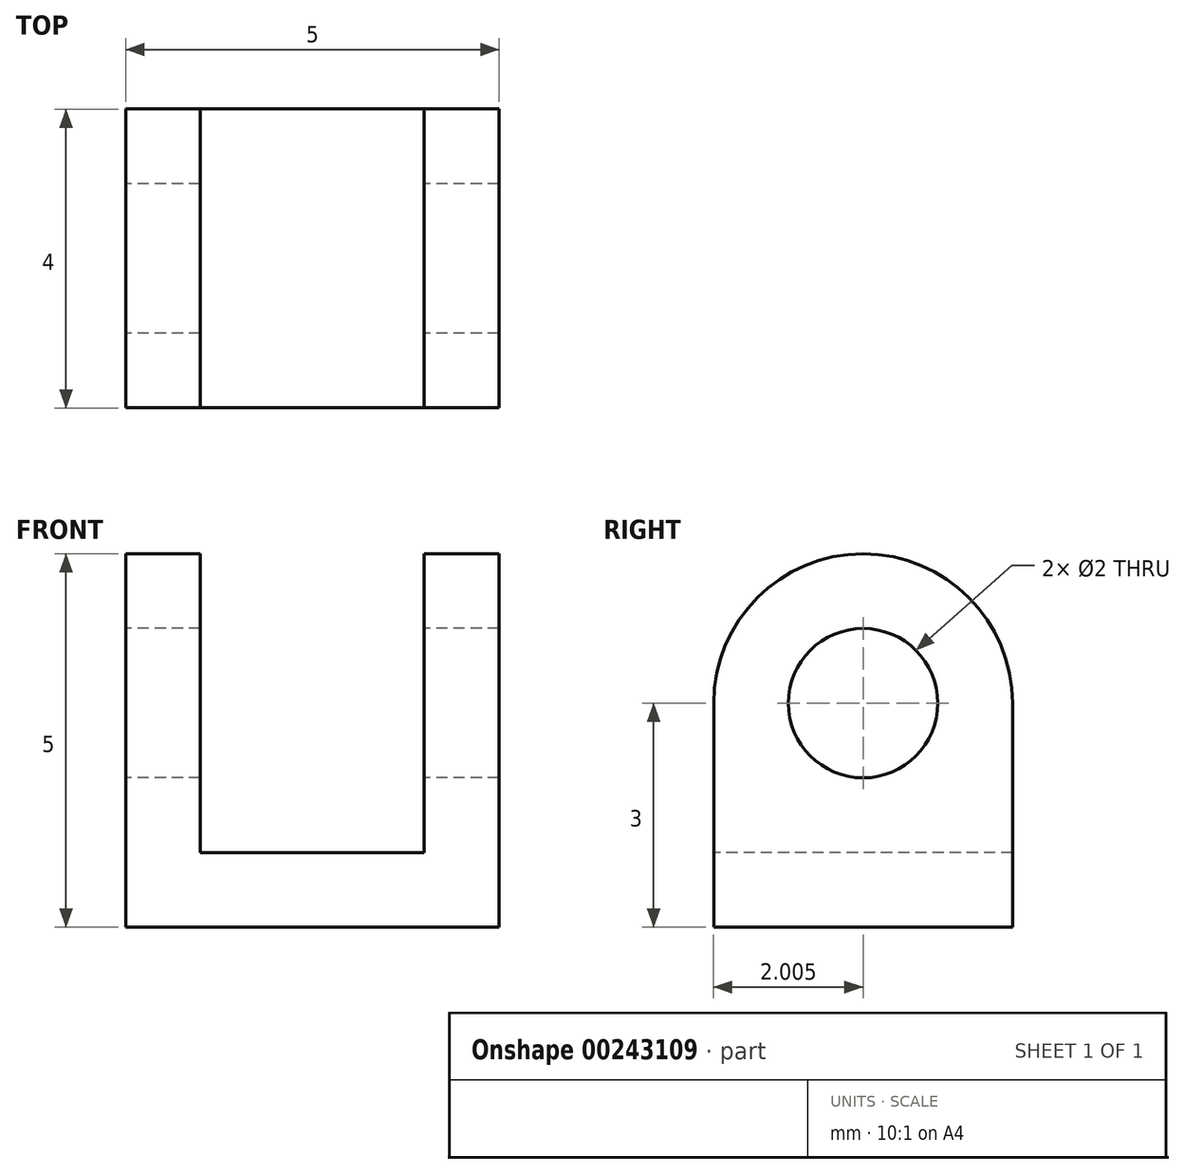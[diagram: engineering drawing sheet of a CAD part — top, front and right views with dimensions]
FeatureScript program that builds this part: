
annotation { "Feature Type Name" : "Feature", "Feature Type Description" : "" }
export const myFeature = defineFeature(function(context is Context, id is Id, definition is map)
    precondition{}
    {
        {
            var Q0;
            Q0=qCreatedBy(makeId("Top.planeOp"),FACE);
            var sketch = newSketch(context, id + "F0", { "sketchPlane" : qUnion([Q0])});
            skLineSegment(sketch, "E0.bottom", {"start": v(31.9, 8.6) * mm, "end": v(36.9, 8.6) * mm});
            skLineSegment(sketch, "E0.top", {"start": v(31.9, 4.6) * mm, "end": v(36.9, 4.6) * mm});
            skLineSegment(sketch, "E0.left", {"start": v(31.9, 8.6) * mm, "end": v(31.9, 4.6) * mm});
            skLineSegment(sketch, "E0.right", {"start": v(36.9, 8.6) * mm, "end": v(36.9, 4.6) * mm});
            skSolve(sketch);
        }
        {
            var Q0;
            Q0=makeQuery(id+"F0.imprint","IMPRINT",FACE,{"disambiguationData":[TD([[makeQuery(id+"F0.imprint","IMPRINT",EDGE,{"derivedFrom":sQuery(id+"F0.wireOp",EDGE,"E0.bottom")}),-1.0]])]});
            extrude(context, id + "F1", {"entities" : qUnion([Q0]), "depth" : 1 * mm});
        }
        {
            var Q0;
            Q0=makeQuery(id+"F1.opExtrude","CAP_FACE",FACE,{"disambiguationData":[OSD([sQuery(id+"F0.wireOp",EDGE,"E0.bottom"),sQuery(id+"F0.wireOp",EDGE,"E0.top"),sQuery(id+"F0.wireOp",EDGE,"E0.left"),sQuery(id+"F0.wireOp",EDGE,"E0.right")])],"isStart":false});
            var sketch = newSketch(context, id + "F2", { "sketchPlane" : qUnion([Q0])});
            skLineSegment(sketch, "E1", {"start": v(32.9, 8.6) * mm, "end": v(32.9, 4.6) * mm});
            skLineSegment(sketch, "E2", {"start": v(35.9, 8.6) * mm, "end": v(35.9, 4.6) * mm});
            skLineSegment(sketch, "E3", {"start": v(32.9, 8.6) * mm, "end": v(35.9, 8.6) * mm});
            skLineSegment(sketch, "E4", {"start": v(32.9, 4.6) * mm, "end": v(35.9, 4.6) * mm});
            skSolve(sketch);
        }
        {
            var Q0;
            Q0 = qSketchRegion(id + "F2", true);
            var Q1;
            Q1 = qConstructionFilter(qBodyType(qCreatedBy(id + "F2" ,EDGE), BodyType.WIRE), ConstructionObject.NO);
            extrude(context, id + "F3", {"entities" : qUnion([Q0]), "surfaceEntities" : qUnion([Q1]), "depth" : 4 * mm});
        }
        {
            var Q0;
            Q0=makeQuery(id+"F3.opExtrude","SWEPT_FACE",FACE,{"disambiguationData":[OSD([sQuery(id+"F2.wireOp",EDGE,"E1")])]});
            var sketch = newSketch(context, id + "F4", { "sketchPlane" : qUnion([Q0])});
            skLineSegment(sketch, "E5.bottom", {"start": v(-8.6, 3) * mm, "end": v(-4.6, 3) * mm});
            skLineSegment(sketch, "E5.top", {"start": v(-8.6, 1) * mm, "end": v(-4.6, 1) * mm});
            skLineSegment(sketch, "E5.left", {"start": v(-8.6, 3) * mm, "end": v(-8.6, 1) * mm});
            skLineSegment(sketch, "E5.right", {"start": v(-4.6, 3) * mm, "end": v(-4.6, 1) * mm});
            skCircle(sketch, "E6", {"center": v(-6.6, 3) * mm, "radius": 2 * mm});
            skSolve(sketch);
        }
        {
            var Q0;
            Q0 = qSketchRegion(id + "F4", true);
            extrude(context, id + "F5", {"entities" : qUnion([Q0]), "operationType" : NewBodyOperationType.ADD, "depth" : 1 * mm});
        }
        {
            var Q0;
            Q0=makeQuery(id+"F3.opExtrude","SWEPT_FACE",FACE,{"disambiguationData":[OSD([sQuery(id+"F2.wireOp",EDGE,"E2")])]});
            var sketch = newSketch(context, id + "F6", { "sketchPlane" : qUnion([Q0])});
            skArc(sketch, "E7.0", {"start": v(4.6, 3) * mm, "mid": v(6.6, 5) * mm, "end": v(8.6, 3) * mm});
            skLineSegment(sketch, "E7.1", {"start": v(8.6, 3) * mm, "end": v(8.6, 1) * mm});
            skLineSegment(sketch, "E7.2", {"start": v(4.6, 3) * mm, "end": v(4.6, 1) * mm});
            skLineSegment(sketch, "E7.3", {"start": v(8.6, 1) * mm, "end": v(4.6, 1) * mm});
            skSolve(sketch);
        }
        {
            var Q0;
            Q0 = qSketchRegion(id + "F6", true);
            extrude(context, id + "F7", {"entities" : qUnion([Q0]), "operationType" : NewBodyOperationType.ADD, "depth" : 1 * mm});
        }
        {
            var Q0;
            Q0=makeQuery(id+"F2.imprint","IMPRINT",FACE,{"disambiguationData":[TD([[makeQuery(id+"F2.imprint","IMPRINT",EDGE,{"derivedFrom":sQuery(id+"F2.wireOp",EDGE,"E1")}),1.0]])]});
            var sketch = newSketch(context, id + "F8", { "sketchPlane" : qUnion([Q0])});
            skPoint(sketch, "E8.0", {"position": v(32.9, 8.6) * mm});
            skPoint(sketch, "E9.0", {"position": v(35.9, 8.6) * mm});
            skPoint(sketch, "E10.0", {"position": v(35.9, 4.6) * mm});
            skPoint(sketch, "E11.0", {"position": v(32.9, 4.6) * mm});
            skLineSegment(sketch, "E12", {"start": v(32.9, 8.6) * mm, "end": v(32.9, 4.6) * mm});
            skLineSegment(sketch, "E13", {"start": v(35.9, 4.6) * mm, "end": v(35.9, 8.6) * mm});
            skLineSegment(sketch, "E14", {"start": v(32.9, 8.6) * mm, "end": v(35.9, 8.6) * mm});
            skLineSegment(sketch, "E15", {"start": v(35.9, 4.6) * mm, "end": v(32.9, 4.6) * mm});
            skSolve(sketch);
        }
        {
            var Q0;
            Q0 = qSketchRegion(id + "F8", true);
            extrude(context, id + "F9", {"entities" : qUnion([Q0]), "operationType" : NewBodyOperationType.REMOVE, "depth" : 25 * mm});
        }
        {
            var Q0;
            Q0=makeQuery(id+"F5.boolean.opBoolean","MERGE",FACE,{"derivedFrom":[makeQuery(id+"F1.opExtrude","SWEPT_FACE",FACE,{"disambiguationData":[OSD([sQuery(id+"F0.wireOp",EDGE,"E0.left")])]}),makeQuery(id+"F5.opExtrude","CAP_FACE",FACE,{"disambiguationData":[OSD([sQuery(id+"F4.wireOp",EDGE,"E5.top"),sQuery(id+"F4.wireOp",EDGE,"E5.left"),sQuery(id+"F4.wireOp",EDGE,"E5.right"),sQuery(id+"F4.wireOp",EDGE,"E6")])],"isStart":false})]});
            var sketch = newSketch(context, id + "F10", { "sketchPlane" : qUnion([Q0])});
            skCircle(sketch, "E16", {"center": v(-6.6, 3) * mm, "radius": 1 * mm});
            skLineSegment(sketch, "E17", {"start": v(-6.6, 5.5) * mm, "end": v(-6.6, 3) * mm, "construction": true});
            skLineSegment(sketch, "E18", {"start": v(-9.1, 3) * mm, "end": v(-6.6, 3) * mm, "construction": true});
            skLineSegment(sketch, "E19", {"start": v(-6.6, 0.5) * mm, "end": v(-6.6, 3) * mm, "construction": true});
            skLineSegment(sketch, "E20", {"start": v(-6.6, 3) * mm, "end": v(-4.1, 3) * mm, "construction": true});
            skSolve(sketch);
        }
        {
            var Q0;
            Q0 = qSketchRegion(id + "F10", true);
            extrude(context, id + "F11", {"entities" : qUnion([Q0]), "operationType" : NewBodyOperationType.REMOVE, "oppositeDirection" : true, "depth" : 25 * mm});
        }
    });
